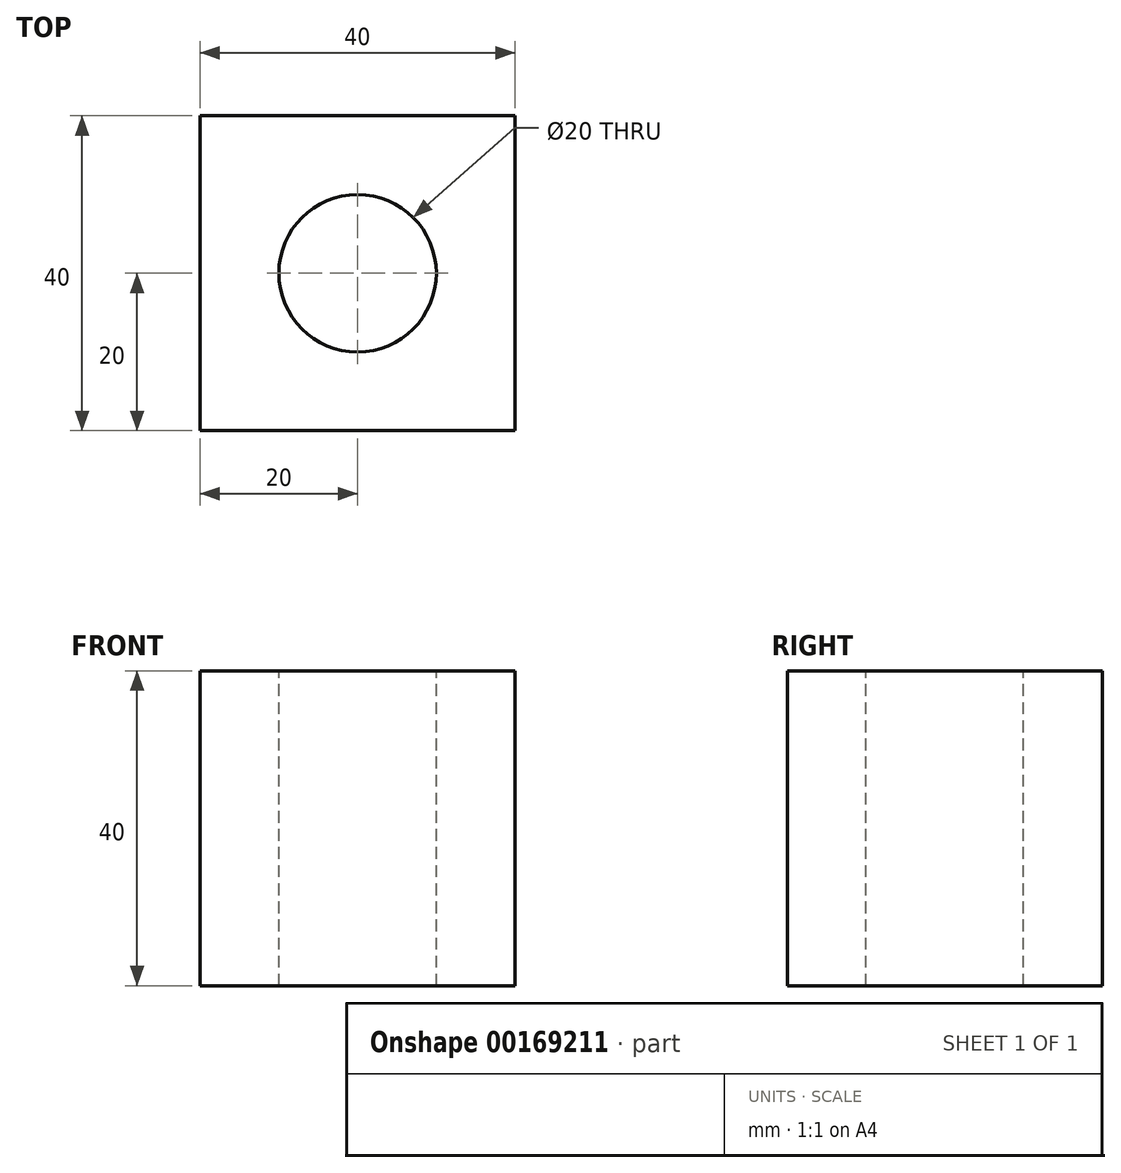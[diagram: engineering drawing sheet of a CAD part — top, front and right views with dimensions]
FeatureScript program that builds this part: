
annotation { "Feature Type Name" : "Feature", "Feature Type Description" : "" }
export const myFeature = defineFeature(function(context is Context, id is Id, definition is map)
    precondition{}
    {
        {
            var Q0;
            Q0=qCreatedBy(makeId("Top.planeOp"),FACE);
            var sketch = newSketch(context, id + "F0", { "sketchPlane" : qUnion([Q0])});
            skLineSegment(sketch, "E0.bottom", {"start": v(20, -20) * mm, "end": v(-20, -20) * mm});
            skLineSegment(sketch, "E0.top", {"start": v(20, 20) * mm, "end": v(-20, 20) * mm});
            skLineSegment(sketch, "E0.left", {"start": v(20, -20) * mm, "end": v(20, 20) * mm});
            skLineSegment(sketch, "E0.right", {"start": v(-20, -20) * mm, "end": v(-20, 20) * mm});
            skPoint(sketch, "E0.middle", {"position": v(0, 0) * mm});
            skSolve(sketch);
        }
        {
            var Q0;
            Q0 = qSketchRegion(id + "F0", true);
            extrude(context, id + "F1", {"entities" : qUnion([Q0]), "depth" : 40 * mm});
        }
        {
            var Q0;
            Q0=makeQuery(id+"F1.opExtrude","CAP_FACE",FACE,{"disambiguationData":[OSD([sQuery(id+"F0.wireOp",EDGE,"E0.bottom"),sQuery(id+"F0.wireOp",EDGE,"E0.top"),sQuery(id+"F0.wireOp",EDGE,"E0.left"),sQuery(id+"F0.wireOp",EDGE,"E0.right")])],"isStart":false});
            var sketch = newSketch(context, id + "F2", { "sketchPlane" : qUnion([Q0])});
            skCircle(sketch, "E1", {"center": v(0, 0) * mm, "radius": 10 * mm});
            skSolve(sketch);
        }
        {
            var Q0;
            Q0 = qSketchRegion(id + "F2", true);
            extrude(context, id + "F3", {"entities" : qUnion([Q0]), "operationType" : NewBodyOperationType.REMOVE, "endBound" : BoundingType.THROUGH_ALL, "oppositeDirection" : true, "depth" : 25 * mm});
        }
    });
